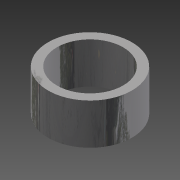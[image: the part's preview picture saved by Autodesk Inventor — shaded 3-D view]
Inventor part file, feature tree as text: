
AUTODESK INVENTOR PART (.ipt)
format: ipt  version: 2015 (Build 190159000, 159)  size: 109,568 bytes
history: native  units: mm
features: sketch x2, other x1, extrude x1, hole x1
ambient origin geometry x8: Origin, YZ Plane, XZ Plane, XY Plane, X Axis, Y Axis, Z Axis, Center Point
bodies: Body1 (feature_tree)
feature tree (5):
  other  "Bryła1"
  extrude  "Wyciągnięcie proste1"  Depth=17.2mm
  hole  "Otwór1"  [1 undecoded]
  sketch  "Szkic1"
  sketch  "Szkic2"
note: 1 required parameter value undecoded (feature->parameter linkage not recoverable at this tier; creation-order binding heuristic only, values carry confidence <= 0.55)
